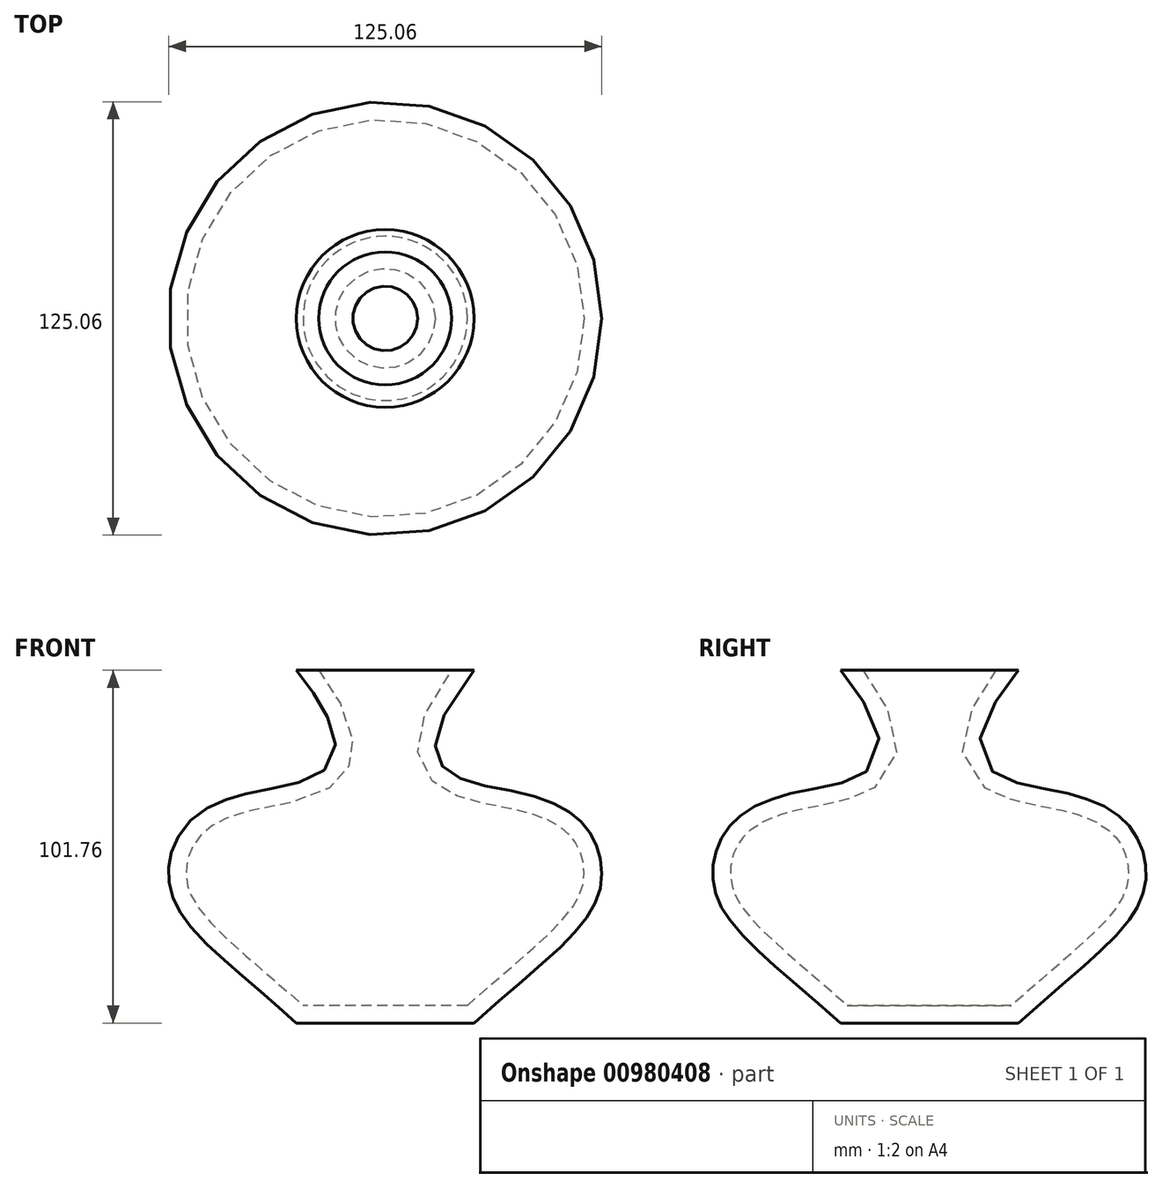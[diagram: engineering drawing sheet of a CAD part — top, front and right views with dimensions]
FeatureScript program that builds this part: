
annotation { "Feature Type Name" : "Feature", "Feature Type Description" : "" }
export const myFeature = defineFeature(function(context is Context, id is Id, definition is map)
    precondition{}
    {
        {
            var Q0;
            Q0=qCreatedBy(makeId("Front.planeOp"),FACE);
            var sketch = newSketch(context, id + "F0", { "sketchPlane" : qUnion([Q0])});
            skLineSegment(sketch, "E0", {"start": v(-35.67, 45.26) * mm, "end": v(-35.67, -56.5) * mm});
            skLineSegment(sketch, "E1", {"start": v(-35.67, -56.5) * mm, "end": v(-10.05, -56.5) * mm});
            skLineSegment(sketch, "E2", {"start": v(-35.67, 45.26) * mm, "end": v(-10.05, 45.26) * mm});
            skFitSpline(sketch, "E3", {"points": [v(-10.05, -56.5) * mm, v(25.39, -20.82) * mm, v(24.3, -3.06) * mm, v(2.59, 10.1) * mm, v(-10.05, 45.26) * mm], "startDerivative": vector(174.2, 155.79) * mm, "endDerivative": vector(278.1, 346.78) * mm});
            skPoint(sketch, "E4.startDerivative.orphan", {"position": v(15.4, 13.8) * mm});
            skPoint(sketch, "E5.1.internal.orphan", {"position": v(22.41, 13.8) * mm});
            skSolve(sketch);
        }
        {
            var Q0;
            Q0=makeQuery(id+"F0.imprint","IMPRINT",FACE,{"disambiguationData":[TD([[makeQuery(id+"F0.imprint","IMPRINT",EDGE,{"derivedFrom":sQuery(id+"F0.wireOp",EDGE,"E0")}),1.0]])]});
            var Q1;
            Q1=sQuery(id+"F0.wireOp",EDGE,"E0");
            revolve(context, id + "F1", {"surfaceOperationType" : NewSurfaceOperationType.NEW, "entities" : qUnion([Q0]), "axis" : qUnion([Q1]), "revolveType" : RevolveType.FULL});
        }
        {
            var Q0;
            Q0=makeQuery(id+"F1.opRevolve","SWEPT_FACE",FACE,{"disambiguationData":[OSD([sQuery(id+"F0.wireOp",EDGE,"E2")])]});
            shell(context, id + "F2", {"entities" : qUnion([Q0]), "thickness" : 5.08 * mm});
        }
    });
